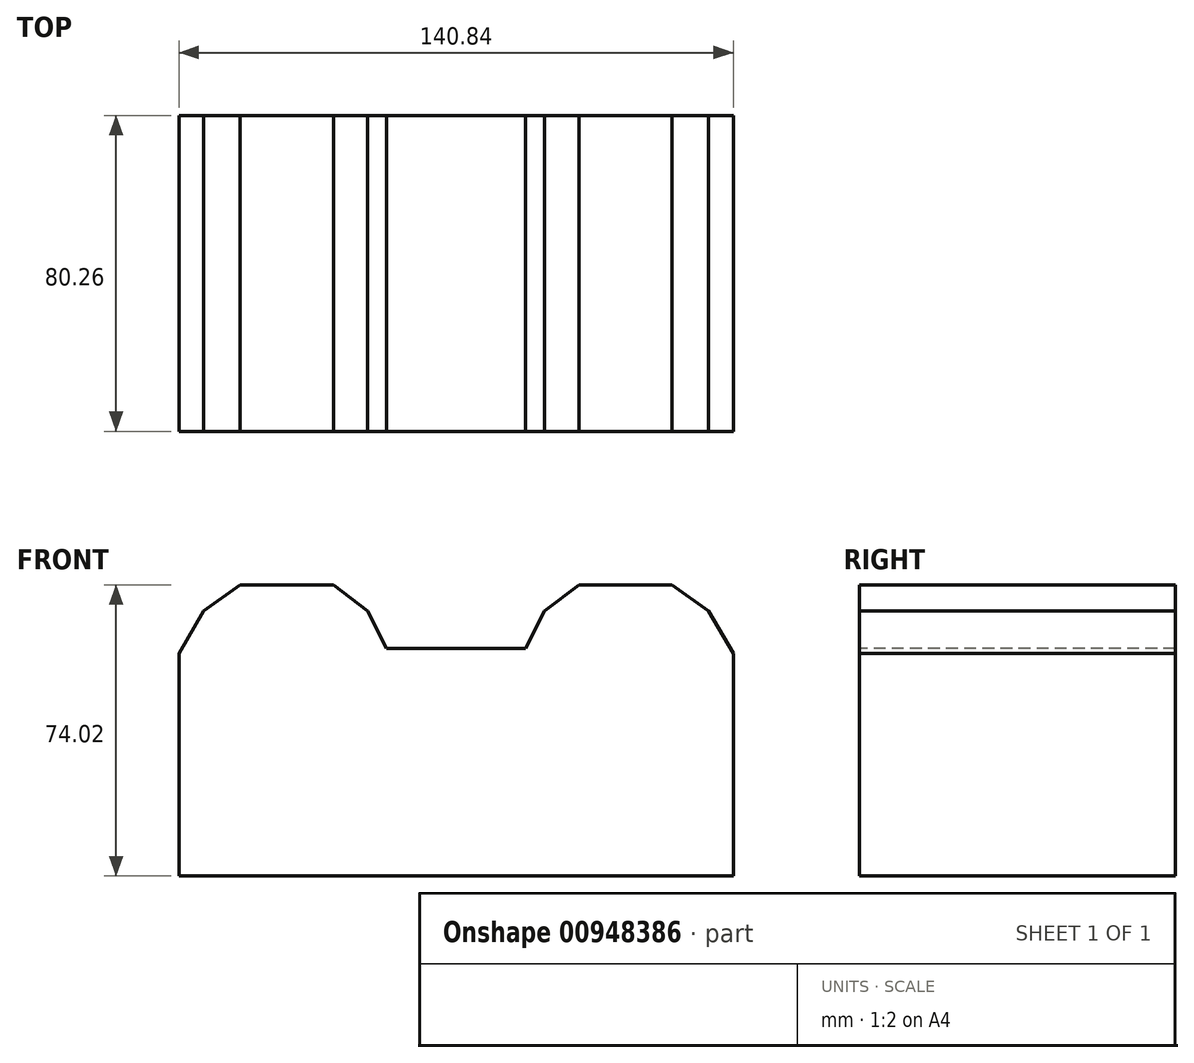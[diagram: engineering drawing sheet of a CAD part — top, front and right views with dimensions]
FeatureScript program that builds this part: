
annotation { "Feature Type Name" : "Feature", "Feature Type Description" : "" }
export const myFeature = defineFeature(function(context is Context, id is Id, definition is map)
    precondition{}
    {
        {
            var Q0;
            Q0=qCreatedBy(makeId("Front.planeOp"),FACE);
            var sketch = newSketch(context, id + "F0", { "sketchPlane" : qUnion([Q0])});
            skLineSegment(sketch, "E0", {"start": v(-63.15, -42.78) * mm, "end": v(0, -42.78) * mm});
            skLineSegment(sketch, "E1", {"start": v(-63.15, -42.78) * mm, "end": v(-63.15, 13.86) * mm});
            skLineSegment(sketch, "E2", {"start": v(-63.15, 13.86) * mm, "end": v(-56.86, 24.65) * mm});
            skLineSegment(sketch, "E3", {"start": v(-56.86, 24.65) * mm, "end": v(-47.57, 31.24) * mm});
            skLineSegment(sketch, "E4", {"start": v(-47.57, 31.24) * mm, "end": v(-23.9, 31.24) * mm});
            skLineSegment(sketch, "E5", {"start": v(-23.9, 31.24) * mm, "end": v(-15.2, 24.65) * mm});
            skLineSegment(sketch, "E6", {"start": v(-15.2, 24.65) * mm, "end": v(-10.41, 15.06) * mm});
            skLineSegment(sketch, "E7", {"start": v(-10.41, 15.06) * mm, "end": v(0, 15.06) * mm});
            skLineSegment(sketch, "E8", {"start": v(0, 15.06) * mm, "end": v(7.27, 15.06) * mm});
            skLineSegment(sketch, "E9", {"start": v(7.27, -42.78) * mm, "end": v(0, -42.78) * mm});
            skLineSegment(sketch, "E10.MirrorCS", {"start": v(24.95, 15.06) * mm, "end": v(14.53, 15.06) * mm});
            skLineSegment(sketch, "E11.MirrorCS", {"start": v(14.53, 15.06) * mm, "end": v(7.27, 15.06) * mm});
            skLineSegment(sketch, "E12.MirrorCS", {"start": v(77.69, -42.78) * mm, "end": v(14.53, -42.78) * mm});
            skLineSegment(sketch, "E13.MirrorCS", {"start": v(7.27, -42.78) * mm, "end": v(14.53, -42.78) * mm});
            skLineSegment(sketch, "E14.MirrorCS", {"start": v(77.69, -42.78) * mm, "end": v(77.69, 13.86) * mm});
            skLineSegment(sketch, "E15.MirrorCS", {"start": v(77.69, 13.86) * mm, "end": v(71.4, 24.65) * mm});
            skLineSegment(sketch, "E16.MirrorCS", {"start": v(71.4, 24.65) * mm, "end": v(62.1, 31.24) * mm});
            skLineSegment(sketch, "E17.MirrorCS", {"start": v(62.1, 31.24) * mm, "end": v(38.43, 31.24) * mm});
            skLineSegment(sketch, "E18.MirrorCS", {"start": v(38.43, 31.24) * mm, "end": v(29.74, 24.65) * mm});
            skLineSegment(sketch, "E19.MirrorCS", {"start": v(29.74, 24.65) * mm, "end": v(24.95, 15.06) * mm});
            skSolve(sketch);
        }
        {
            var Q0;
            Q0=makeQuery(id+"F0.imprint","IMPRINT",FACE,{"disambiguationData":[TD([[makeQuery(id+"F0.imprint","IMPRINT",EDGE,{"derivedFrom":sQuery(id+"F0.wireOp",EDGE,"E0")}),1.0]])]});
            extrude(context, id + "F1", {"entities" : qUnion([Q0]), "oppositeDirection" : true, "depth" : 80.26 * mm, "offsetDistance" : 25.4 * mm});
        }
    });
